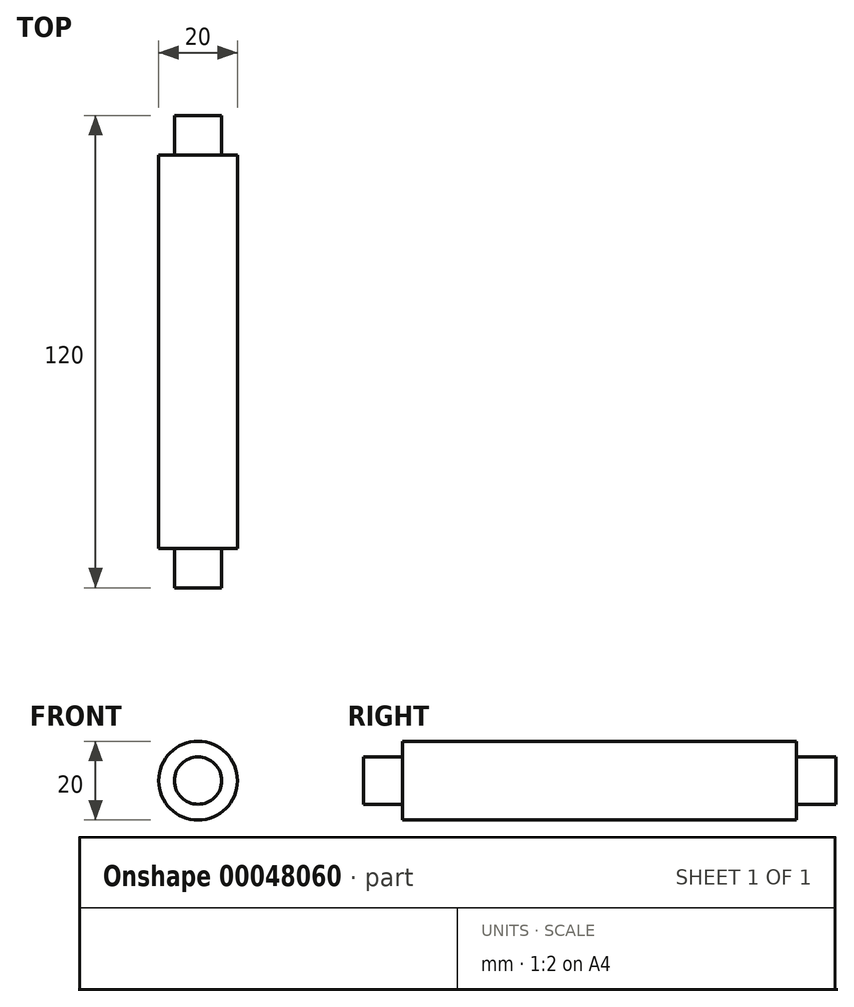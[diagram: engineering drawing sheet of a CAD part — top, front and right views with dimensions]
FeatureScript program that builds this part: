
annotation { "Feature Type Name" : "Feature", "Feature Type Description" : "" }
export const myFeature = defineFeature(function(context is Context, id is Id, definition is map)
    precondition{}
    {
        {
            var Q0;
            Q0=qCreatedBy(makeId("Top.planeOp"),FACE);
            var sketch = newSketch(context, id + "F0", { "sketchPlane" : qUnion([Q0])});
            skLineSegment(sketch, "E0", {"start": v(0, 0) * mm, "end": v(0, 120) * mm});
            skLineSegment(sketch, "E1", {"start": v(0, 120) * mm, "end": v(-6, 120) * mm});
            skLineSegment(sketch, "E2", {"start": v(-6, 120) * mm, "end": v(-6, 110) * mm});
            skLineSegment(sketch, "E3", {"start": v(-6, 110) * mm, "end": v(-10, 110) * mm});
            skLineSegment(sketch, "E4", {"start": v(-10, 110) * mm, "end": v(-10, 10) * mm});
            skLineSegment(sketch, "E5", {"start": v(-10, 10) * mm, "end": v(-6, 10) * mm});
            skLineSegment(sketch, "E6", {"start": v(-6, 10) * mm, "end": v(-6, 0) * mm});
            skLineSegment(sketch, "E7", {"start": v(-6, 0) * mm, "end": v(0, 0) * mm});
            skSolve(sketch);
        }
        {
            var Q0;
            Q0=makeQuery(id+"F0.imprint","IMPRINT",FACE,{"disambiguationData":[TD([[makeQuery(id+"F0.imprint","IMPRINT",EDGE,{"derivedFrom":sQuery(id+"F0.wireOp",EDGE,"E0")}),1.0]])]});
            var Q1;
            Q1=sQuery(id+"F0.wireOp",EDGE,"E0");
            revolve(context, id + "F1", {"entities" : qUnion([Q0]), "axis" : qUnion([Q1]), "revolveType" : RevolveType.FULL});
        }
    });
